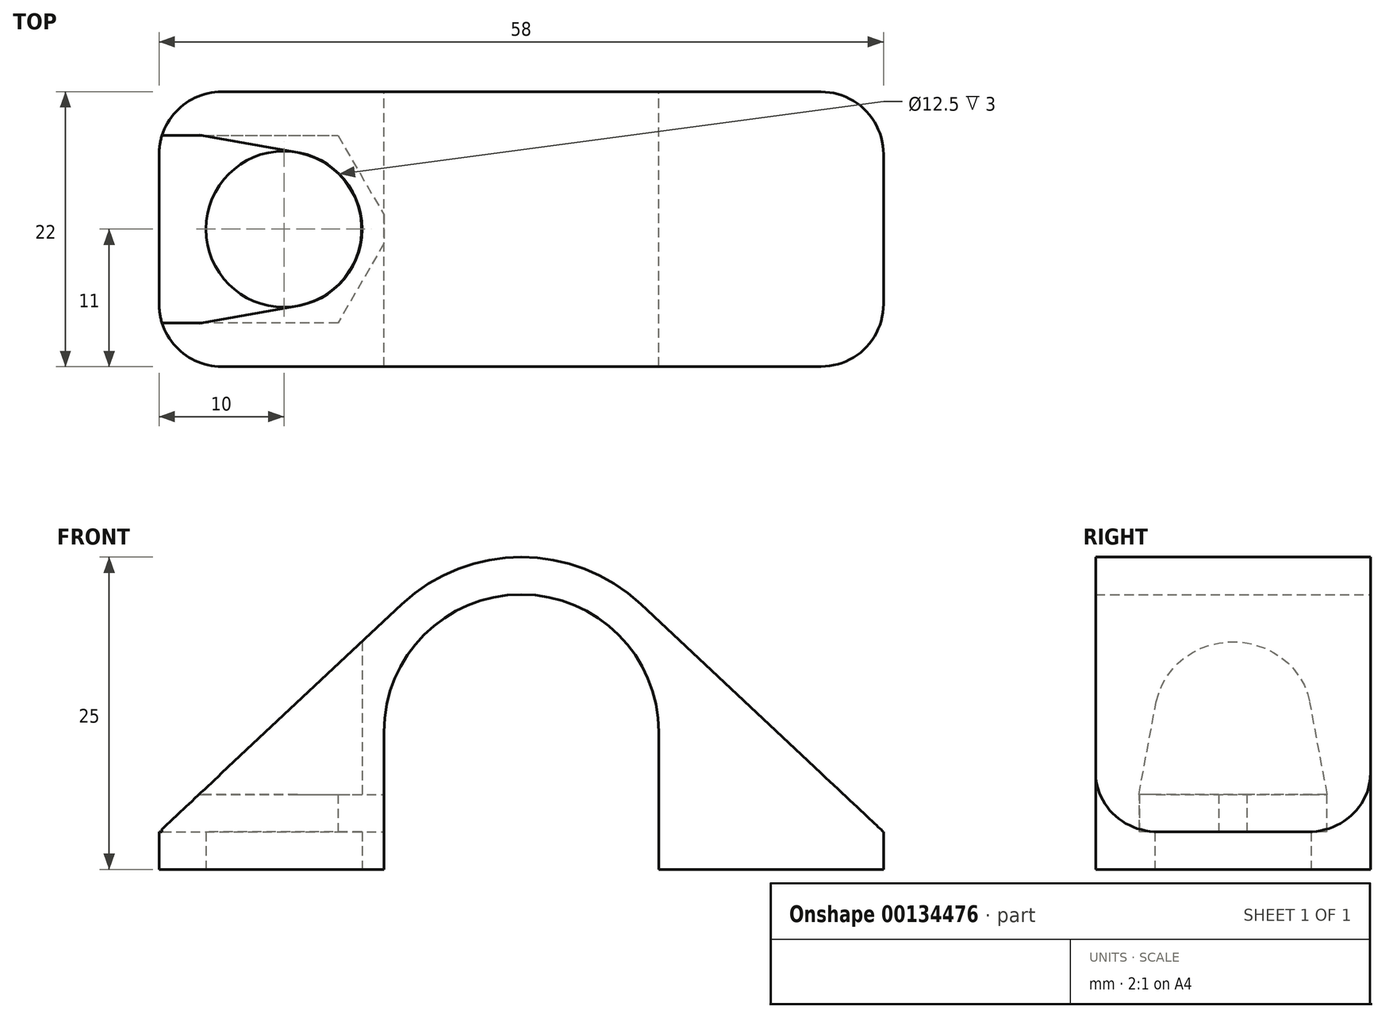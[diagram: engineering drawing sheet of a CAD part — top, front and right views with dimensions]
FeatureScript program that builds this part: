
annotation { "Feature Type Name" : "Feature", "Feature Type Description" : "" }
export const myFeature = defineFeature(function(context is Context, id is Id, definition is map)
    precondition{}
    {
        {
            var Q0;
            Q0=qCreatedBy(makeId("Top.planeOp"),FACE);
            var sketch = newSketch(context, id + "F0", { "sketchPlane" : qUnion([Q0])});
            skLineSegment(sketch, "E0.bottom", {"start": v(11, -17.54) * mm, "end": v(-11, -17.54) * mm});
            skLineSegment(sketch, "E0.top", {"start": v(11, 17.54) * mm, "end": v(-11, 17.54) * mm});
            skLineSegment(sketch, "E0.left", {"start": v(11, -17.54) * mm, "end": v(11, 17.54) * mm});
            skLineSegment(sketch, "E0.right", {"start": v(-11, -17.54) * mm, "end": v(-11, 17.54) * mm});
            skPoint(sketch, "E0.middle", {"position": v(0, 0) * mm});
            skCircle(sketch, "E1.cCircle", {"center": v(-19, 0) * mm, "radius": 7.5 * mm, "construction": true});
            skLineSegment(sketch, "E1.0", {"start": v(-14.67, -7.5) * mm, "end": v(-23.33, -7.5) * mm});
            skLineSegment(sketch, "E1.1", {"start": v(-23.33, -7.5) * mm, "end": v(-27.66, 0) * mm});
            skLineSegment(sketch, "E1.2", {"start": v(-27.66, 0) * mm, "end": v(-23.33, 7.5) * mm});
            skLineSegment(sketch, "E1.3", {"start": v(-23.33, 7.5) * mm, "end": v(-14.67, 7.5) * mm});
            skLineSegment(sketch, "E1.4", {"start": v(-14.67, 7.5) * mm, "end": v(-10.34, 0) * mm});
            skLineSegment(sketch, "E1.5", {"start": v(-10.34, 0) * mm, "end": v(-14.67, -7.5) * mm});
            skPoint(sketch, "E1.0.midPoint", {"position": v(-19, -7.5) * mm});
            skSolve(sketch);
        }
        {
            var Q0;
            Q0=qCreatedBy(makeId("Front.planeOp"),FACE);
            var sketch = newSketch(context, id + "F1", { "sketchPlane" : qUnion([Q0])});
            skArc(sketch, "E2", {"start": v(11, 11) * mm, "mid": v(0, 22) * mm, "end": v(-11, 11) * mm});
            skLineSegment(sketch, "E3", {"start": v(-11, 11) * mm, "end": v(-11, 0) * mm});
            skLineSegment(sketch, "E4", {"start": v(-11, 0) * mm, "end": v(-29, 0) * mm});
            skLineSegment(sketch, "E5", {"start": v(11, 11) * mm, "end": v(11, 0) * mm});
            skLineSegment(sketch, "E6", {"start": v(11, 0) * mm, "end": v(29, 0) * mm});
            skArc(sketch, "E7.0", {"start": v(9.58, 21.21) * mm, "mid": v(0, 25) * mm, "end": v(-9.58, 21.21) * mm});
            skLineSegment(sketch, "E8", {"start": v(-19, 8.5) * mm, "end": v(-19, -9.59) * mm, "construction": true});
            skLineSegment(sketch, "E9", {"start": v(-29, 0) * mm, "end": v(-29, 3) * mm});
            skLineSegment(sketch, "E10", {"start": v(-29, 3) * mm, "end": v(-9.58, 21.21) * mm});
            skLineSegment(sketch, "E11", {"start": v(29, 0) * mm, "end": v(29, 3) * mm});
            skLineSegment(sketch, "E12", {"start": v(29, 3) * mm, "end": v(9.58, 21.21) * mm});
            skSolve(sketch);
        }
        {
            var Q0;
            Q0 = qSketchRegion(id + "F1", true);
            extrude(context, id + "F2", {"entities" : qUnion([Q0]), "depth" : 22 * mm, "symmetric" : true});
        }
        {
            var Q0;
            Q0=qCreatedBy(makeId("Top.planeOp"),FACE);
            var Q1;
            Q1=makeQuery(id+"F2.opExtrude","CAP_VERTEX",VERTEX,{"disambiguationData":[OSD([sQuery(id+"F1.wireOp",EDGE,"E9"),sQuery(id+"F1.wireOp",EDGE,"E10")])],"isStart":false});
            cPlane(context, id + "F3", {"entities" : qUnion([Q0, Q1]), "cplaneType" : CPlaneType.PLANE_POINT, "offset" : 25 * mm, "width" : 150 * mm, "height" : 150 * mm});
        }
        {
            var Q0;
            Q0=qCreatedBy(id+"F3.planeOp",FACE);
            var sketch = newSketch(context, id + "F4", { "sketchPlane" : qUnion([Q0])});
            skLineSegment(sketch, "E13.0", {"start": v(-14.67, 7.5) * mm, "end": v(-10.34, 0) * mm});
            skLineSegment(sketch, "E14.0", {"start": v(-10.34, 0) * mm, "end": v(-14.67, -7.5) * mm});
            skLineSegment(sketch, "E15.0", {"start": v(-37.18, 7.5) * mm, "end": v(-14.67, 7.5) * mm});
            skLineSegment(sketch, "E16.0", {"start": v(-14.67, -7.5) * mm, "end": v(-37.18, -7.5) * mm});
            skLineSegment(sketch, "E17", {"start": v(-37.18, -7.5) * mm, "end": v(-37.18, 7.5) * mm});
            skPoint(sketch, "E18.orphan", {"position": v(-23.33, 7.5) * mm});
            skPoint(sketch, "E19.orphan", {"position": v(-23.33, -7.5) * mm});
            skSolve(sketch);
        }
        {
            var Q0;
            Q0 = qSketchRegion(id + "F4", true);
            extrude(context, id + "F5", {"entities" : qUnion([Q0]), "operationType" : NewBodyOperationType.REMOVE, "depth" : 3 * mm});
        }
        {
            var Q0;
            Q0=qCreatedBy(makeId("Top.planeOp"),FACE);
            var sketch = newSketch(context, id + "F6", { "sketchPlane" : qUnion([Q0])});
            skCircle(sketch, "E20.0", {"center": v(-19, 0) * mm, "radius": 7.5 * mm, "construction": true});
            skCircle(sketch, "E21", {"center": v(-19, 0) * mm, "radius": 6.25 * mm});
            skSolve(sketch);
        }
        {
            var Q0;
            Q0 = qSketchRegion(id + "F6", true);
            extrude(context, id + "F7", {"entities" : qUnion([Q0]), "operationType" : NewBodyOperationType.REMOVE, "endBound" : BoundingType.THROUGH_ALL, "depth" : 25 * mm});
        }
        {
            var Q0;
            Q0=makeQuery(id+"F5.boolean.opBoolean","COPY",FACE,{"derivedFrom":makeQuery(id+"F5.opExtrude","CAP_FACE",FACE,{"disambiguationData":[OSD([sQuery(id+"F4.wireOp",EDGE,"E13.0"),sQuery(id+"F4.wireOp",EDGE,"E14.0"),sQuery(id+"F4.wireOp",EDGE,"E15.0"),sQuery(id+"F4.wireOp",EDGE,"E16.0"),sQuery(id+"F4.wireOp",EDGE,"E17")])],"isStart":false})});
            var sketch = newSketch(context, id + "F8", { "sketchPlane" : qUnion([Q0])});
            skArc(sketch, "E22.0", {"start": v(-17.91, -6.16) * mm, "mid": v(-12.75, 0) * mm, "end": v(-17.91, 6.16) * mm});
            skLineSegment(sketch, "E23", {"start": v(-17.91, -6.16) * mm, "end": v(-27, -7.76) * mm});
            skLineSegment(sketch, "E24", {"start": v(-27, -7.76) * mm, "end": v(-27, 7.76) * mm});
            skLineSegment(sketch, "E25", {"start": v(-17.91, 6.16) * mm, "end": v(-27, 7.76) * mm});
            skPoint(sketch, "E26.orphan", {"position": v(-24.93, -1.97) * mm});
            skPoint(sketch, "E27.orphan", {"position": v(-24.93, 1.97) * mm});
            skSolve(sketch);
        }
        {
            var Q0;
            Q0 = qSketchRegion(id + "F8", true);
            extrude(context, id + "F9", {"entities" : qUnion([Q0]), "operationType" : NewBodyOperationType.REMOVE, "endBound" : BoundingType.THROUGH_ALL, "oppositeDirection" : true, "depth" : 25 * mm});
        }
        {
            var Q0;
            Q0=makeQuery(id+"F2.opExtrude","CAP_EDGE",EDGE,{"disambiguationData":[OSD([sQuery(id+"F1.wireOp",EDGE,"E9")])],"isStart":false});
            var Q1;
            Q1=makeQuery(id+"F2.opExtrude","CAP_EDGE",EDGE,{"disambiguationData":[OSD([sQuery(id+"F1.wireOp",EDGE,"E9")])],"isStart":true});
            var Q2;
            Q2=makeQuery(id+"F2.opExtrude","CAP_EDGE",EDGE,{"disambiguationData":[OSD([sQuery(id+"F1.wireOp",EDGE,"E11")])],"isStart":false});
            var Q3;
            Q3=makeQuery(id+"F2.opExtrude","CAP_EDGE",EDGE,{"disambiguationData":[OSD([sQuery(id+"F1.wireOp",EDGE,"E11")])],"isStart":true});
            fillet(context, id + "F10", {"entities" : qUnion([Q0, Q1, Q2, Q3]), "radius" : 5 * mm, "tangentPropagation" : true, "allowEdgeOverflow" : false});
        }
    });
